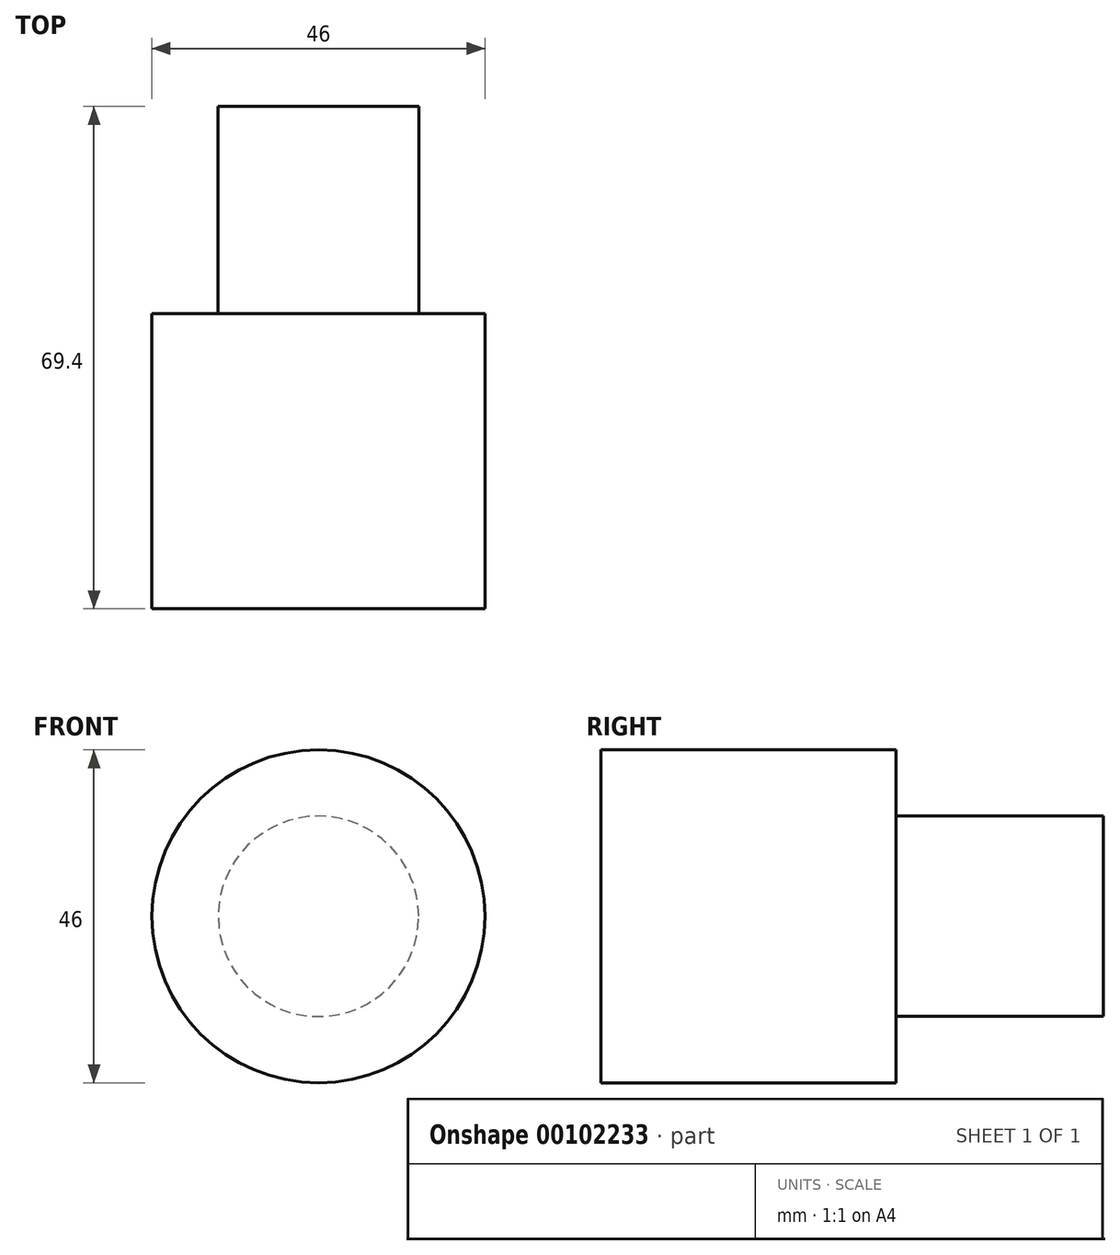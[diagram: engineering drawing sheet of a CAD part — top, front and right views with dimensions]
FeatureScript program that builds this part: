
annotation { "Feature Type Name" : "Feature", "Feature Type Description" : "" }
export const myFeature = defineFeature(function(context is Context, id is Id, definition is map)
    precondition{}
    {
        {
            var Q0;
            Q0=qCreatedBy(makeId("Right.planeOp"),FACE);
            var sketch = newSketch(context, id + "F0", { "sketchPlane" : qUnion([Q0])});
            skLineSegment(sketch, "E0.bottom", {"start": v(0, 0) * mm, "end": v(-40.76, 0) * mm});
            skLineSegment(sketch, "E0.top", {"start": v(0, 23) * mm, "end": v(-40.76, 23) * mm});
            skLineSegment(sketch, "E0.left", {"start": v(0, 0) * mm, "end": v(0, 23) * mm});
            skLineSegment(sketch, "E0.right", {"start": v(-40.76, 0) * mm, "end": v(-40.76, 23) * mm});
            skLineSegment(sketch, "E1.bottom", {"start": v(0, 0) * mm, "end": v(0, 0) * mm});
            skLineSegment(sketch, "E1.top", {"start": v(0, 23) * mm, "end": v(0, 23) * mm});
            skLineSegment(sketch, "E2.bottom", {"start": v(0, 0) * mm, "end": v(28.64, 0) * mm});
            skLineSegment(sketch, "E2.top", {"start": v(0, 13.85) * mm, "end": v(28.64, 13.85) * mm});
            skLineSegment(sketch, "E2.left", {"start": v(0, 0) * mm, "end": v(0, 13.85) * mm});
            skLineSegment(sketch, "E2.right", {"start": v(28.64, 0) * mm, "end": v(28.64, 13.85) * mm});
            skSolve(sketch);
        }
        {
            var Q0;
            Q0=makeQuery(id+"F0.imprint","IMPRINT",FACE,{"disambiguationData":[TD([[makeQuery(id+"F0.imprint","IMPRINT",EDGE,{"derivedFrom":sQuery(id+"F0.wireOp",EDGE,"E0.bottom")}),-1.0]])]});
            var Q1;
            Q1=makeQuery(id+"F0.imprint","IMPRINT",FACE,{"disambiguationData":[TD([[makeQuery(id+"F0.imprint","IMPRINT",EDGE,{"derivedFrom":sQuery(id+"F0.wireOp",EDGE,"E2.bottom")}),1.0]])]});
            var Q2;
            Q2=sQuery(id+"F0.wireOp",EDGE,"E0.bottom");
            revolve(context, id + "F1", {"entities" : qUnion([Q0, Q1]), "axis" : qUnion([Q2]), "revolveType" : RevolveType.FULL});
        }
    });
